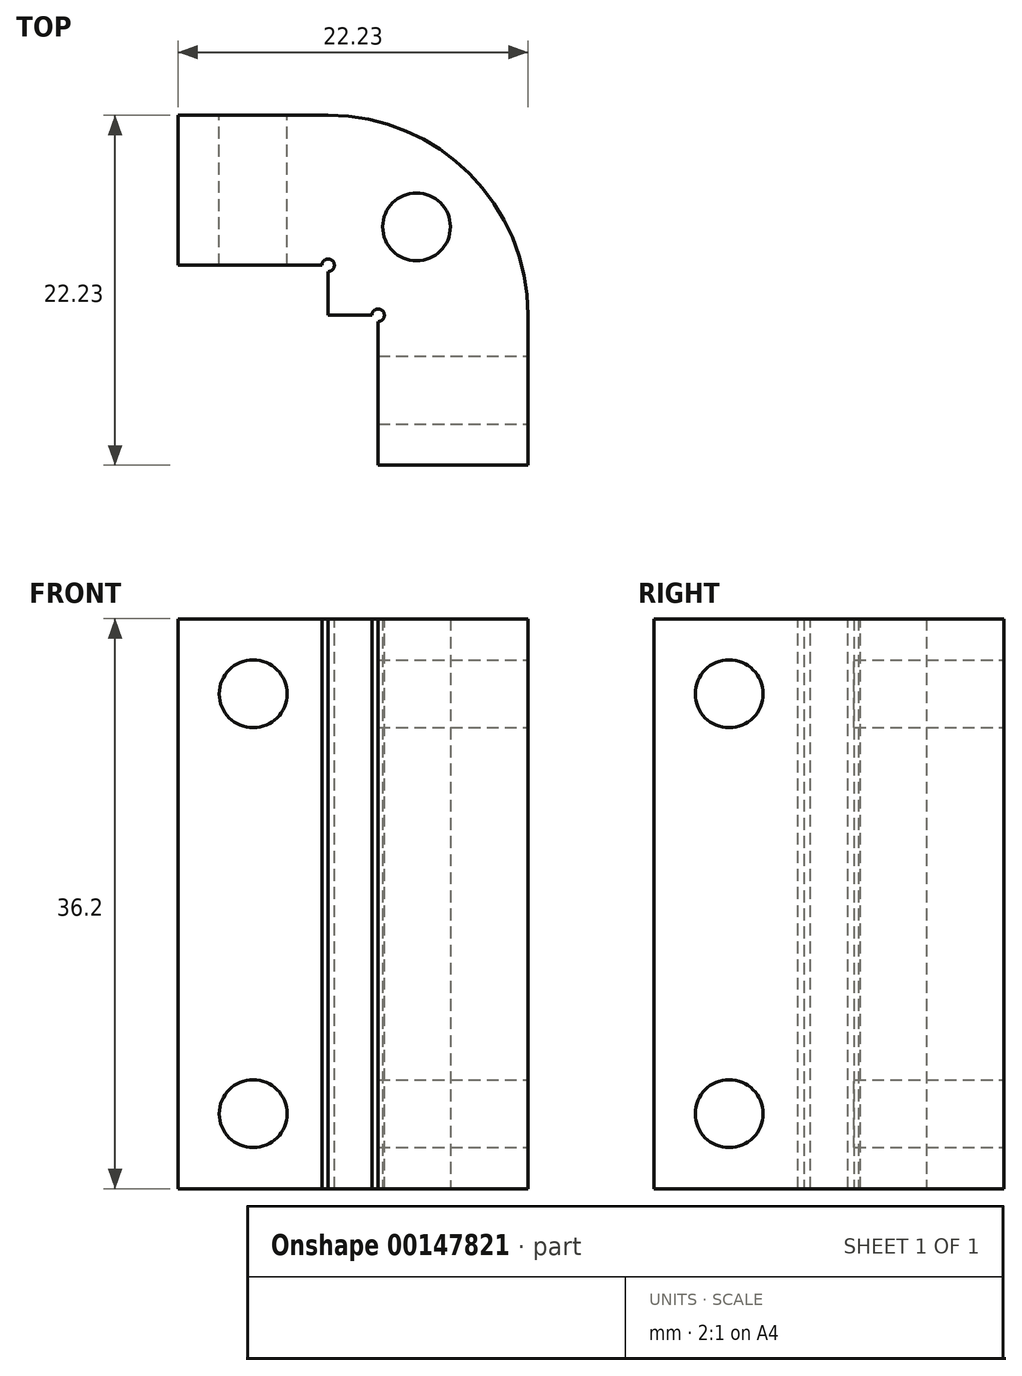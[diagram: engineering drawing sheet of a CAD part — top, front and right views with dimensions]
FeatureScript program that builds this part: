
annotation { "Feature Type Name" : "Feature", "Feature Type Description" : "" }
export const myFeature = defineFeature(function(context is Context, id is Id, definition is map)
    precondition{}
    {
        {
            var Q0;
            Q0=qCreatedBy(makeId("Top.planeOp"),FACE);
            var sketch = newSketch(context, id + "F0", { "sketchPlane" : qUnion([Q0])});
            skLineSegment(sketch, "E0.bottom", {"start": v(0, 0) * mm, "end": v(-9.53, 0) * mm});
            skLineSegment(sketch, "E0.top", {"start": v(0, -9.52) * mm, "end": v(-9.52, -9.53) * mm});
            skLineSegment(sketch, "E0.right", {"start": v(-9.53, 0) * mm, "end": v(-9.53, -9.53) * mm});
            skArc(sketch, "E1", {"start": v(12.7, -12.7) * mm, "mid": v(8.98, -3.72) * mm, "end": v(0, 0) * mm});
            skLineSegment(sketch, "E2.bottom", {"start": v(12.7, -22.23) * mm, "end": v(3.18, -22.23) * mm});
            skLineSegment(sketch, "E2.left", {"start": v(12.7, -22.22) * mm, "end": v(12.7, -12.7) * mm});
            skLineSegment(sketch, "E2.right", {"start": v(3.18, -22.23) * mm, "end": v(3.18, -12.7) * mm});
            skLineSegment(sketch, "E3", {"start": v(0, -9.52) * mm, "end": v(0, -12.7) * mm});
            skLineSegment(sketch, "E4", {"start": v(3.18, -12.7) * mm, "end": v(0, -12.7) * mm});
            skCircle(sketch, "E5", {"center": v(5.61, -7.09) * mm, "radius": 4.76 * mm, "construction": true});
            skLineSegment(sketch, "E6", {"start": v(0, -12.7) * mm, "end": v(0, -12.7) * mm});
            skLineSegment(sketch, "E7", {"start": v(5.61, -7.09) * mm, "end": v(0, -12.7) * mm, "construction": true});
            skCircle(sketch, "E8", {"center": v(5.61, -7.09) * mm, "radius": 2.15 * mm});
            skSolve(sketch);
        }
        {
            var Q0;
            Q0=qSketchRegion(id+"F0",true);
            extrude(context, id + "F1", {"entities" : qUnion([Q0]), "depth" : 36.2 * mm});
        }
        {
            var Q0;
            Q0=makeQuery(id+"F1.opExtrude","SWEPT_FACE",FACE,{"disambiguationData":[OSD([sQuery(id+"F0.wireOp",EDGE,"E0.bottom")])]});
            var sketch = newSketch(context, id + "F2", { "sketchPlane" : qUnion([Q0])});
            skLineSegment(sketch, "E9.bottom", {"start": v(4.76, 36.2) * mm, "end": v(9.53, 36.2) * mm, "construction": true});
            skLineSegment(sketch, "E9.top", {"start": v(4.76, 31.43) * mm, "end": v(9.53, 31.43) * mm, "construction": true});
            skLineSegment(sketch, "E9.left", {"start": v(4.76, 36.2) * mm, "end": v(4.76, 31.43) * mm, "construction": true});
            skLineSegment(sketch, "E9.right", {"start": v(9.53, 36.2) * mm, "end": v(9.53, 31.43) * mm, "construction": true});
            skLineSegment(sketch, "E10.bottom", {"start": v(4.76, 0) * mm, "end": v(9.53, 0) * mm, "construction": true});
            skLineSegment(sketch, "E10.top", {"start": v(4.76, 4.76) * mm, "end": v(9.53, 4.76) * mm, "construction": true});
            skLineSegment(sketch, "E10.left", {"start": v(4.76, 0) * mm, "end": v(4.76, 4.76) * mm, "construction": true});
            skLineSegment(sketch, "E10.right", {"start": v(9.53, 0) * mm, "end": v(9.53, 4.76) * mm, "construction": true});
            skCircle(sketch, "E11", {"center": v(4.76, 31.43) * mm, "radius": 2.15 * mm});
            skCircle(sketch, "E12", {"center": v(4.76, 4.76) * mm, "radius": 2.15 * mm});
            skSolve(sketch);
        }
        {
            var Q0;
            Q0=qSketchRegion(id+"F2",true);
            var Q1;
            Q1=makeQuery(id+"F1.opExtrude","SWEPT_FACE",FACE,{"disambiguationData":[OSD([sQuery(id+"F0.wireOp",EDGE,"E0.top")])]});
            extrude(context, id + "F3", {"entities" : qUnion([Q0]), "operationType" : NewBodyOperationType.REMOVE, "endBound" : BoundingType.UP_TO_SURFACE, "oppositeDirection" : true, "endBoundEntityFace" : qUnion([Q1]), "depth" : 25.4 * mm});
        }
        {
            var Q0;
            Q0=makeQuery(id+"F1.opExtrude","SWEPT_FACE",FACE,{"disambiguationData":[OSD([sQuery(id+"F0.wireOp",EDGE,"E2.left")])]});
            var sketch = newSketch(context, id + "F4", { "sketchPlane" : qUnion([Q0])});
            skLineSegment(sketch, "E13.bottom", {"start": v(-17.46, 36.2) * mm, "end": v(-22.23, 36.2) * mm, "construction": true});
            skLineSegment(sketch, "E13.top", {"start": v(-17.46, 31.43) * mm, "end": v(-22.23, 31.43) * mm, "construction": true});
            skLineSegment(sketch, "E13.left", {"start": v(-17.46, 36.2) * mm, "end": v(-17.46, 31.43) * mm, "construction": true});
            skLineSegment(sketch, "E13.right", {"start": v(-22.23, 36.2) * mm, "end": v(-22.23, 31.43) * mm, "construction": true});
            skLineSegment(sketch, "E14.bottom", {"start": v(-17.46, 0) * mm, "end": v(-22.23, 0) * mm, "construction": true});
            skLineSegment(sketch, "E14.top", {"start": v(-17.46, 4.76) * mm, "end": v(-22.23, 4.76) * mm, "construction": true});
            skLineSegment(sketch, "E14.left", {"start": v(-17.46, 0) * mm, "end": v(-17.46, 4.76) * mm, "construction": true});
            skLineSegment(sketch, "E14.right", {"start": v(-22.23, 0) * mm, "end": v(-22.23, 4.76) * mm, "construction": true});
            skCircle(sketch, "E15", {"center": v(-17.46, 31.43) * mm, "radius": 2.15 * mm});
            skCircle(sketch, "E16", {"center": v(-17.46, 4.76) * mm, "radius": 2.15 * mm});
            skSolve(sketch);
        }
        {
            var Q0;
            Q0=qSketchRegion(id+"F4",true);
            var Q1;
            Q1=makeQuery(id+"F1.opExtrude","SWEPT_FACE",FACE,{"disambiguationData":[OSD([sQuery(id+"F0.wireOp",EDGE,"E2.right")])]});
            extrude(context, id + "F5", {"entities" : qUnion([Q0]), "operationType" : NewBodyOperationType.REMOVE, "endBound" : BoundingType.UP_TO_SURFACE, "oppositeDirection" : true, "endBoundEntityFace" : qUnion([Q1]), "depth" : 25.4 * mm});
        }
        {
            var Q0;
            Q0=makeQuery(id+"F1.opExtrude","CAP_FACE",FACE,{"disambiguationData":[OSD([sQuery(id+"F0.wireOp",EDGE,"E0.bottom"),sQuery(id+"F0.wireOp",EDGE,"E0.top"),sQuery(id+"F0.wireOp",EDGE,"E0.right"),sQuery(id+"F0.wireOp",EDGE,"E1"),sQuery(id+"F0.wireOp",EDGE,"E2.bottom"),sQuery(id+"F0.wireOp",EDGE,"E2.left"),sQuery(id+"F0.wireOp",EDGE,"E2.right"),sQuery(id+"F0.wireOp",EDGE,"E3"),sQuery(id+"F0.wireOp",EDGE,"E4"),sQuery(id+"F0.wireOp",EDGE,"E8")])],"isStart":false});
            var sketch = newSketch(context, id + "F6", { "sketchPlane" : qUnion([Q0])});
            skCircle(sketch, "E17", {"center": v(0, -9.52) * mm, "radius": 0.4 * mm});
            skCircle(sketch, "E18", {"center": v(3.18, -12.7) * mm, "radius": 0.4 * mm});
            skSolve(sketch);
        }
        {
            var Q0;
            Q0=qSketchRegion(id+"F6",true);
            var Q1;
            Q1=makeQuery(id+"F1.opExtrude","CAP_FACE",FACE,{"disambiguationData":[OSD([sQuery(id+"F0.wireOp",EDGE,"E0.bottom"),sQuery(id+"F0.wireOp",EDGE,"E0.top"),sQuery(id+"F0.wireOp",EDGE,"E0.right"),sQuery(id+"F0.wireOp",EDGE,"E1"),sQuery(id+"F0.wireOp",EDGE,"E2.bottom"),sQuery(id+"F0.wireOp",EDGE,"E2.left"),sQuery(id+"F0.wireOp",EDGE,"E2.right"),sQuery(id+"F0.wireOp",EDGE,"E3"),sQuery(id+"F0.wireOp",EDGE,"E4"),sQuery(id+"F0.wireOp",EDGE,"E8")])],"isStart":true});
            extrude(context, id + "F7", {"entities" : qUnion([Q0]), "operationType" : NewBodyOperationType.REMOVE, "endBound" : BoundingType.UP_TO_SURFACE, "oppositeDirection" : true, "endBoundEntityFace" : qUnion([Q1]), "depth" : 25.4 * mm});
        }
    });
